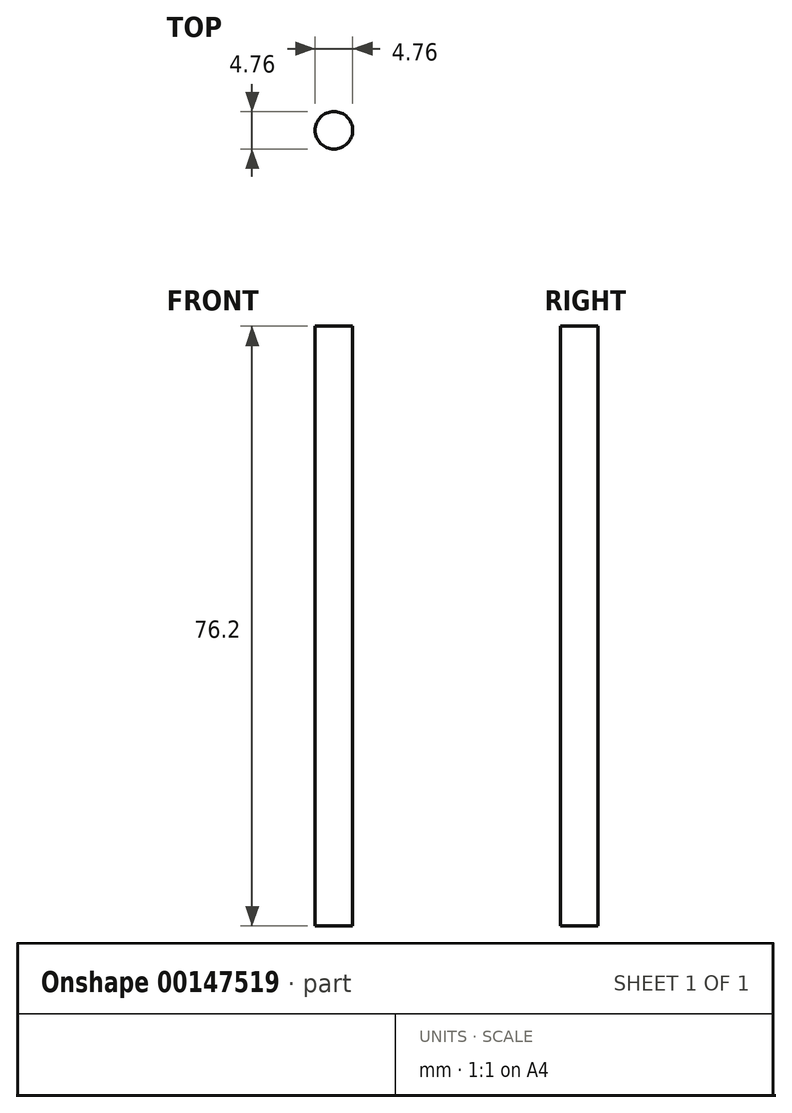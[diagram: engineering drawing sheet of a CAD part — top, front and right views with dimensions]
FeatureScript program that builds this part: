
annotation { "Feature Type Name" : "Feature", "Feature Type Description" : "" }
export const myFeature = defineFeature(function(context is Context, id is Id, definition is map)
    precondition{}
    {
        {
            var Q0;
            Q0=qCreatedBy(makeId("Top.planeOp"),FACE);
            var sketch = newSketch(context, id + "F0", { "sketchPlane" : qUnion([Q0])});
            skCircle(sketch, "E0", {"center": v(0, 0) * mm, "radius": 2.38 * mm});
            skSolve(sketch);
        }
        {
            var Q0;
            Q0=qSketchRegion(id+"F0",true);
            extrude(context, id + "F1", {"entities" : qUnion([Q0]), "depth" : 76.2 * mm});
        }
    });
